# Revit family: Haier-1U140S2SN1FB
name_source: partatom
category: 机械设备
revit_build: Autodesk Revit 2018 (Build: 20170223_1515(x64)
units: mm (PartAtom-declared; Revit-internal decimal feet)

## family parameters
OmniClass 标题 = Air Handling Units
OmniClass 编号 = 23.75.35.14
共享 = 否
加载时剪切的空心 = 否
圆形连接件大小 = 使用直径
基于工作平面 = 否
总是垂直 = 是
房间计算点 = 否
零件类型 = 标准

## types (1)
- 1U140S2SN1FB
    Bracket = White,
    Button = silver gray
    Compressor Type = Twin rotary
    CompressorDrive = Inverter driven
    Electrical Supply Type = 3 /380-415/50/60HZ
    External Tempreture Operating Limits Cooling = -10～46℃
    External Tempreture Operating Limits Heating = -15～24℃
    Heating capacity = 15KW
    Model Number = 1U140S2SN1FB
    Nominal Height = 1130mm
    Nominal Length = 1050mm
    Nominal Width = 485mm
    Nominal frequency range = 50/60 HZ
    Output cooling = 13 kW
    Output heating = 15 kW
    Pipe interface = copper
    RatedVoltage = 3 /380-415V
    Refrigerant gas pipe size = 16
    Refrigerant liquid pipe size = 10  [stored 0.0328084 ft]
    Refrigerant pipe = copper
    Size = 1050x485x1130mm
    Sound power level = 72dB
    Sound pressure level = 58dB
    Structure = White,
    UnitDepth = 485
    UnitHeight = 1130
    UnitWidth = 1050
    Weight = 85kg
    refrigerant = R32
    制造商 = Haier
    型号 = 1U140S2SN1FA
1U140S2SN1FA
1U140S2SN1FA
1U140S2SN1FB

note: [stored X ft] marks values corroborated as IEEE doubles in the binary element streams (Revit-internal decimal feet)
